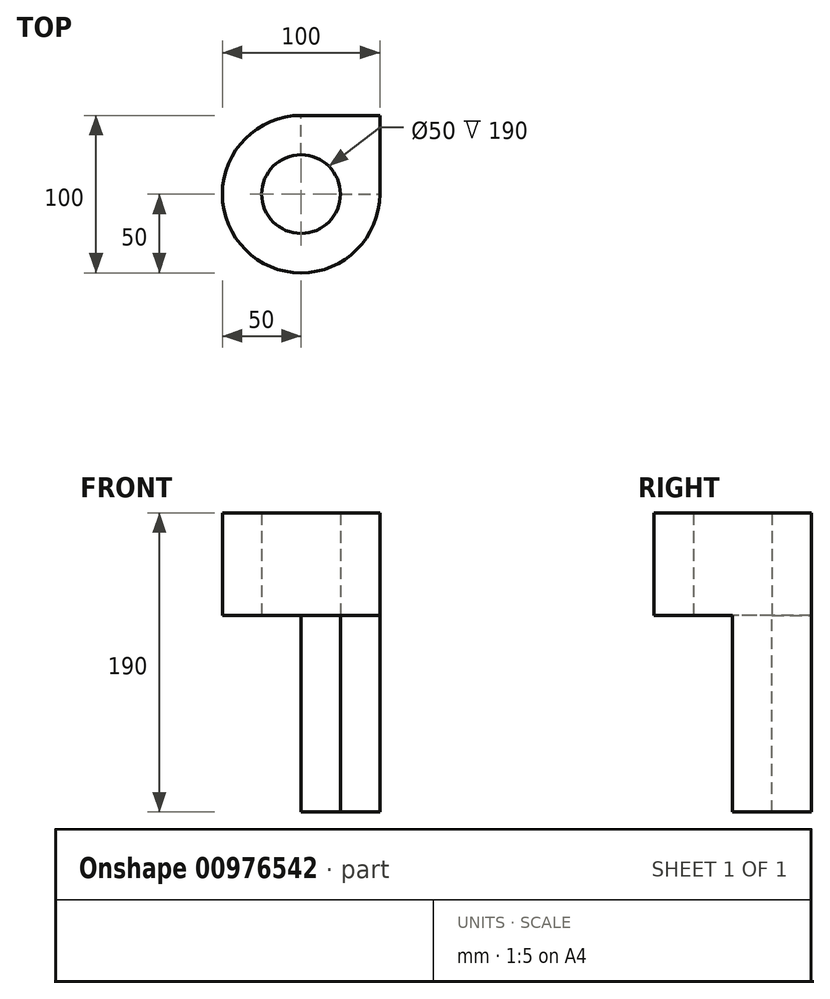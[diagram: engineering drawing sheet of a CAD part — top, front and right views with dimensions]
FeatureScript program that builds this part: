
annotation { "Feature Type Name" : "Feature", "Feature Type Description" : "" }
export const myFeature = defineFeature(function(context is Context, id is Id, definition is map)
    precondition{}
    {
        {
            var Q0;
            Q0=qCreatedBy(makeId("Top.planeOp"),FACE);
            var sketch = newSketch(context, id + "F0", { "sketchPlane" : qUnion([Q0])});
            skLineSegment(sketch, "E0.bottom", {"start": v(0, 0) * mm, "end": v(50, 0) * mm});
            skLineSegment(sketch, "E0.top", {"start": v(0, 50) * mm, "end": v(50, 50) * mm});
            skLineSegment(sketch, "E0.left", {"start": v(0, 0) * mm, "end": v(0, 50) * mm});
            skLineSegment(sketch, "E0.right", {"start": v(50, 0) * mm, "end": v(50, 50) * mm});
            skCircle(sketch, "E1", {"center": v(0, 0) * mm, "radius": 50 * mm});
            skCircle(sketch, "E2", {"center": v(0, 0) * mm, "radius": 25 * mm});
            skSolve(sketch);
        }
        {
            var Q0;
            {var subQ1=sQuery(id+"F0.wireOp",EDGE,"E0.bottom");var subQ3=sQuery(id+"F0.wireOp",EDGE,"E2");var subQ4=makeQuery(id+"F0.imprint","INTERSECT",VERTEX,{"derivedFrom":[subQ1,subQ3]});Q0=makeQuery(id+"F0.imprint","IMPRINT",FACE,{"disambiguationData":[TD([[makeQuery(id+"F0.imprint","IMPRINT",EDGE,{"disambiguationData":[TD([[subQ4,1.0]])],"derivedFrom":subQ3}),-1.0]])]});}
            var Q1;
            Q1 = qSketchRegion(id + "F0", true);
            var Q2;
            {var subQ0=sQuery(id+"F0.wireOp",EDGE,"E0.top");Q2=makeQuery(id+"F0.imprint","IMPRINT",FACE,{"disambiguationData":[TD([[makeQuery(id+"F0.imprint","IMPRINT",EDGE,{"derivedFrom":subQ0}),-1.0]])]});}
            var Q3;
            {var subQ1=sQuery(id+"F0.wireOp",EDGE,"E0.bottom");var subQ3=sQuery(id+"F0.wireOp",EDGE,"E2");var subQ4=makeQuery(id+"F0.imprint","INTERSECT",VERTEX,{"derivedFrom":[subQ1,subQ3]});Q3=makeQuery(id+"F0.imprint","IMPRINT",FACE,{"disambiguationData":[TD([[makeQuery(id+"F0.imprint","IMPRINT",EDGE,{"disambiguationData":[TD([[subQ4,-1.0]])],"derivedFrom":subQ3}),-1.0]])]});}
            extrude(context, id + "F1", {"entities" : qUnion([Q0, Q1, Q2, Q3]), "depth" : 65 * mm, "offsetDistance" : 25 * mm});
        }
        {
            var Q0;
            {var subQ1=sQuery(id+"F0.wireOp",EDGE,"E0.bottom");var subQ3=sQuery(id+"F0.wireOp",EDGE,"E2");var subQ4=makeQuery(id+"F0.imprint","INTERSECT",VERTEX,{"derivedFrom":[subQ1,subQ3]});Q0=makeQuery(id+"F0.imprint","IMPRINT",FACE,{"disambiguationData":[TD([[makeQuery(id+"F0.imprint","IMPRINT",EDGE,{"disambiguationData":[TD([[subQ4,-1.0]])],"derivedFrom":subQ3}),-1.0]])]});}
            var Q1;
            {var subQ0=sQuery(id+"F0.wireOp",EDGE,"E0.top");Q1=makeQuery(id+"F0.imprint","IMPRINT",FACE,{"disambiguationData":[TD([[makeQuery(id+"F0.imprint","IMPRINT",EDGE,{"derivedFrom":subQ0}),-1.0]])]});}
            extrude(context, id + "F2", {"entities" : qUnion([Q0, Q1]), "operationType" : NewBodyOperationType.ADD, "oppositeDirection" : true, "depth" : 125 * mm, "offsetDistance" : 25 * mm});
        }
    });
